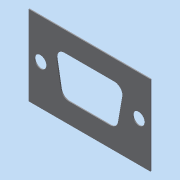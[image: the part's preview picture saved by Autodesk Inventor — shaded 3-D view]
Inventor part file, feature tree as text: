
AUTODESK INVENTOR PART (.ipt)
format: ipt  version: 2016 (Build 200138000, 138)  size: 99,840 bytes
history: native  units: in
note: dims shown in document units (in); Inventor stores cm internally (conversion verified against a paired STEP export)
features: extrude x1, sketch x1
ambient origin geometry x8: Origin, YZ Plane, XZ Plane, XY Plane, X Axis, Y Axis, Z Axis, Center Point
bodies: Solid1 (feature_tree)
feature tree (2):
  extrude  "Extrusion1"  Depth=0.8in
  sketch  "Sketch1"  dims[d0=1.22in d1=0.8in d2=0.0687in d4=0.4in d5=0.0687in d6=0.2799in d7=0.2in d8=0.08in d9=0.08in d10=0.08in d11=0.08in d12=0.66in d13=0.984in d14=0.12in d15=0.12in d16=0.118in d17=0.4in d18=0.4in d19=0.01in d20=0.0in]
